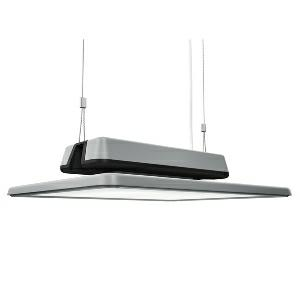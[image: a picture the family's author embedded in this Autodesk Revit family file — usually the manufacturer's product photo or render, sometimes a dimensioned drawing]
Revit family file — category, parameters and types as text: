
# Revit family: acaneo_-_hial_20000_850_n_dali_00734201_db19
name_source: partatom
category: Lighting Fixtures
units: mm (PartAtom-declared; Revit-internal decimal feet)

## family parameters
Cut with Voids When Loaded = No
Host = Face
Light Source = No
Part Type = Normal
Room Calculation Point = No
Round Connector Dimension = Use Diameter
Shared = No

## types (1)
- ACANEO - HIAL 20000/850/N/DALI (1 x LED, 22000 lm, 5000K)
    Apparent Load = 140 VA
    Approval mark = CE
    CIE Flux Codes = 84 97 100 100 100
    Color Rendering = 80-89
    Color Temperature = 5000K
    Control Gear = Electronic ballast
    Default Elevation = 1800 mm
    Description = HIAL 20000/850/N/DALI|High bay luminaire|light source: LED|work equipment: Adjustable electronic ballast, digital DALI|connected load: 220-240 V, 50/60 Hz|Power consumption: approx. 140 W|power factor: approx. 0,951|luminous flux: 22000 lm|luminous efficacy: 157 lm/W|colour temperature: Cold white, ca. 5000 K|color rendering index (CRI): >= 80|chromaticity tolerance:  3 SDCM|System of protection: IP 65|class of protection: I|technology: Continuously dimmable|luminaire body|material: Aluminium|surface: Powder coatet|colour: White aluminium|lamp cover: Acrylic (PMMA), Clear|weight (net): approx. 8.2 kg|mains lead: Built-in plug RST 20i5 Einbau|Fastening: Available separately|Accessory: Junction box (RST 20i5)|minimum ambient temperature: -30 ░C|maximum ambient temperature: 70 ░C|glare control: Optics|unified glare rating(4H 8H): <=  22|
    Frequency = 50 Hz, 60 Hz
    Height = 125 mm
    Lamp = 1 x LED
    Lamp Light Flux = 22000 lm
    Lamp count = 1
    Length = 480 mm
    Luminous efficacy = 157 lm/W
    Manufacturer = Waldmann
    ModVariant = No
    Model = 00734201
    Mounting Place = Ceiling
    Mounting Type = Pendant
    Number of Poles = 1
    OnlyDefault = Yes
    Power Factor = 1
    Product Name = ACANEO - HIAL 20000/850/N/DALI
    Product group = High bay luminaire (industry)
    ProductGroupID = 901
    Protection Class = Protection class I
    Protection Degree = IP 65
    RLX_Detail_Level = 1
    RLX_Emergency_Light_Flux = 0 lm
    RLX_Emergency_Type = 0
    RLX_Emergency_Type_DB = No
    RlxData = <blob elided: 30369 chars, md5=1ce99334>
    Socket = socket
    Standby Power = 0 W
    System Light Flux = 22000 lm
    System Power = 140 W
    Type Comments = Product without accessories
    Type Image = acaneo-hial.jpg
    URL = http://relux.com
    VarID = ---
    Voltage = 230 V
    Voltage Range = 110-120 V, 220-240 V
    Weight = 0.00 kg
    Width = 405 mm

## geometry (parser evidence)
native form markers: Blend x4, Sweep x9
no freeform markers — native parametric forms only
